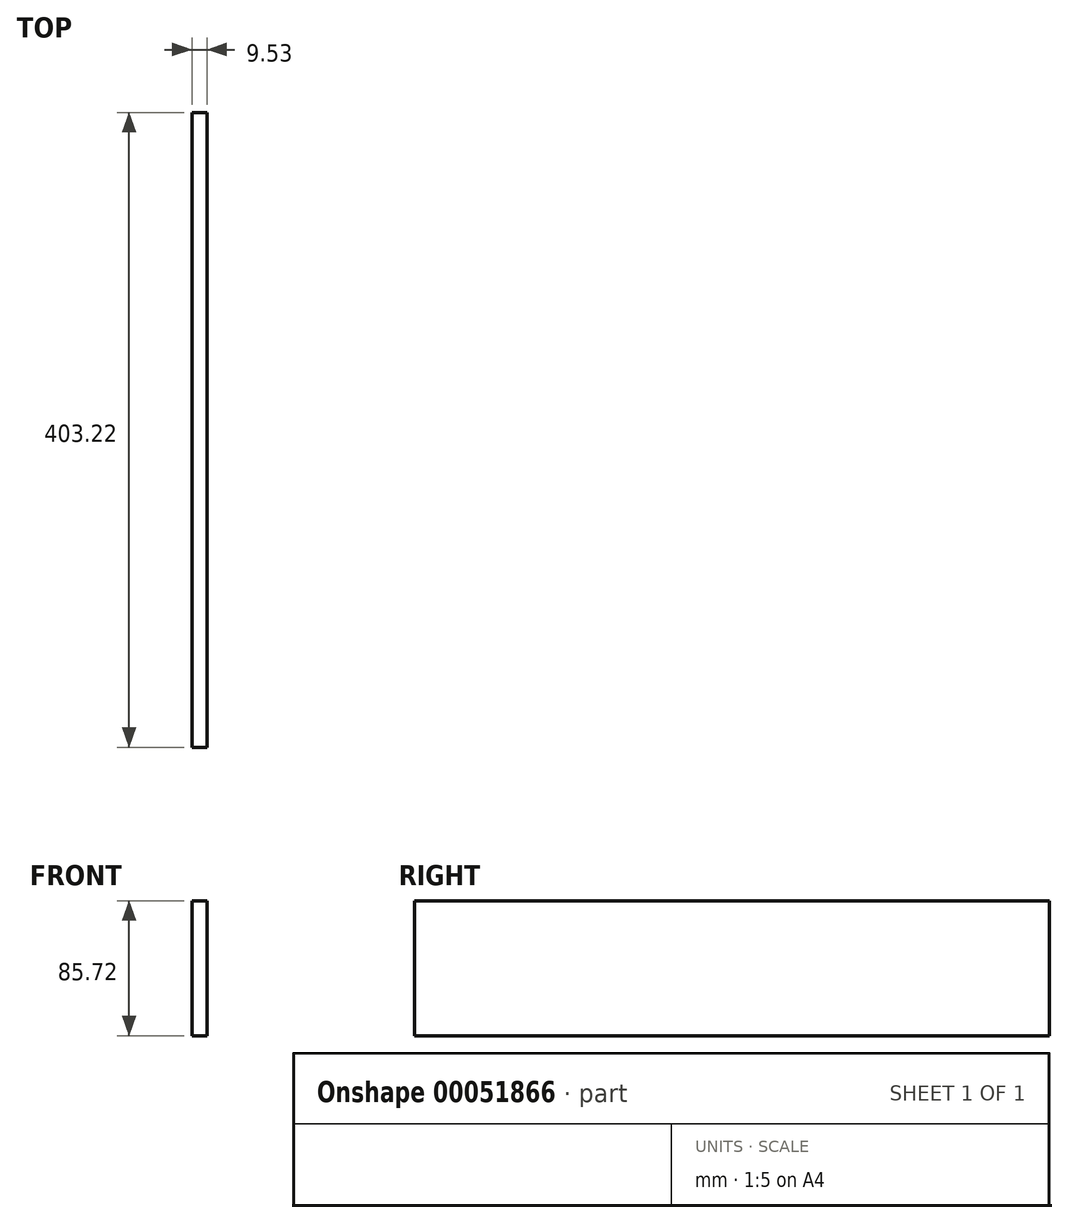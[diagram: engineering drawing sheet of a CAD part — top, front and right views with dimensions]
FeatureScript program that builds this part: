
annotation { "Feature Type Name" : "Feature", "Feature Type Description" : "" }
export const myFeature = defineFeature(function(context is Context, id is Id, definition is map)
    precondition{}
    {
        {
            var Q0;
            Q0=qCreatedBy(makeId("Right.planeOp"),FACE);
            var sketch = newSketch(context, id + "F0", { "sketchPlane" : qUnion([Q0])});
            skLineSegment(sketch, "E0.bottom", {"start": v(-177.8, 38.1) * mm, "end": v(225.43, 38.1) * mm});
            skLineSegment(sketch, "E0.top", {"start": v(-177.8, -47.62) * mm, "end": v(225.43, -47.62) * mm});
            skLineSegment(sketch, "E0.left", {"start": v(-177.8, 38.1) * mm, "end": v(-177.8, -47.62) * mm});
            skLineSegment(sketch, "E0.right", {"start": v(225.43, 38.1) * mm, "end": v(225.43, -47.62) * mm});
            skSolve(sketch);
        }
        {
            var Q0;
            Q0=makeQuery(id+"F0.imprint","IMPRINT",FACE,{"disambiguationData":[TD([[makeQuery(id+"F0.imprint","IMPRINT",EDGE,{"derivedFrom":sQuery(id+"F0.wireOp",EDGE,"E0.bottom")}),-1.0]])]});
            extrude(context, id + "F1", {"entities" : qUnion([Q0]), "depth" : 9.52 * mm});
        }
    });
